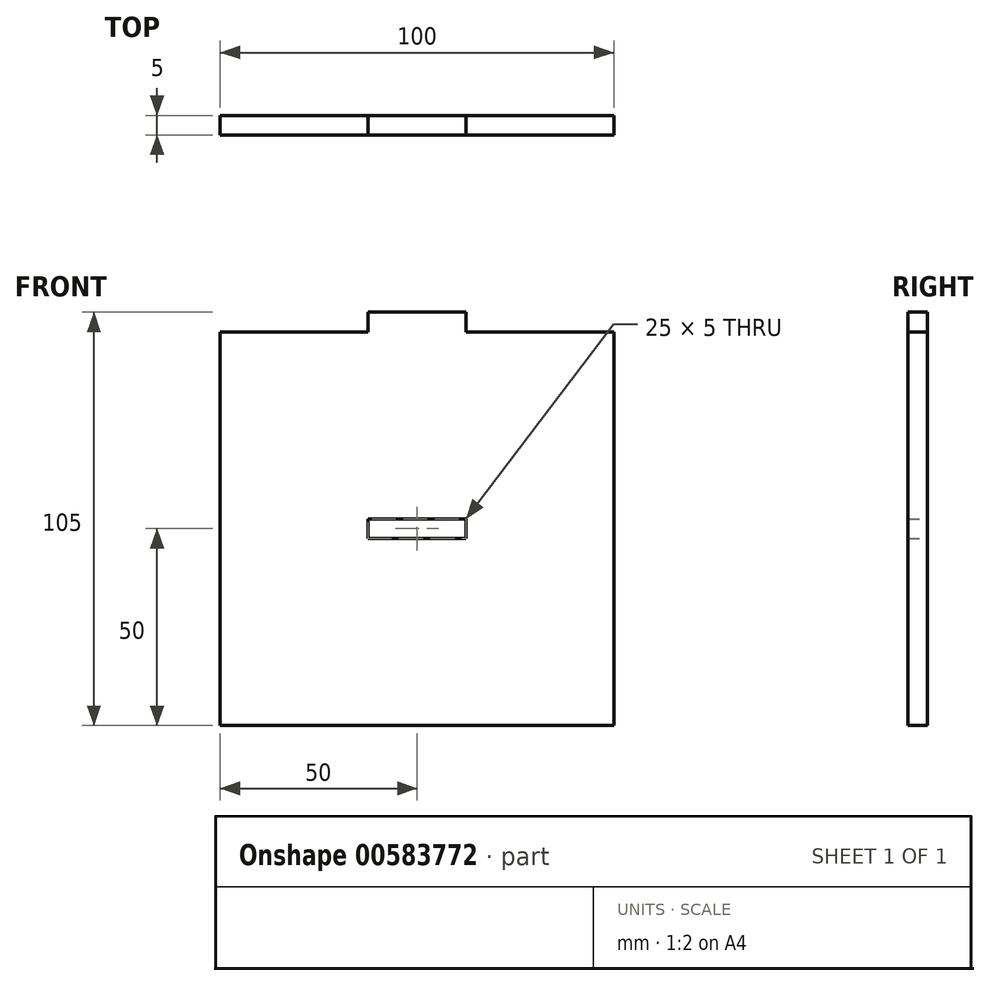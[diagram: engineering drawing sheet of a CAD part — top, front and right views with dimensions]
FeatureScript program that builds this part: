
annotation { "Feature Type Name" : "Feature", "Feature Type Description" : "" }
export const myFeature = defineFeature(function(context is Context, id is Id, definition is map)
    precondition{}
    {
        {
            var Q0;
            Q0=qCreatedBy(makeId("Front.planeOp"),FACE);
            var sketch = newSketch(context, id + "F0", { "sketchPlane" : qUnion([Q0])});
            skLineSegment(sketch, "E0", {"start": v(-62.5, 52.5) * mm, "end": v(-62.5, -47.5) * mm});
            skLineSegment(sketch, "E1", {"start": v(-62.5, -47.5) * mm, "end": v(37.5, -47.5) * mm});
            skLineSegment(sketch, "E2", {"start": v(37.5, -47.5) * mm, "end": v(37.5, 52.5) * mm});
            skLineSegment(sketch, "E3", {"start": v(37.5, 52.5) * mm, "end": v(0, 52.5) * mm});
            skLineSegment(sketch, "E4", {"start": v(0, 52.5) * mm, "end": v(0, 57.5) * mm});
            skLineSegment(sketch, "E5", {"start": v(0, 57.5) * mm, "end": v(-25, 57.5) * mm});
            skLineSegment(sketch, "E6", {"start": v(-25, 57.5) * mm, "end": v(-25, 52.5) * mm});
            skLineSegment(sketch, "E7", {"start": v(-25, 52.5) * mm, "end": v(-62.5, 52.5) * mm});
            skLineSegment(sketch, "E8.left", {"start": v(-58.91, 2.5) * mm, "end": v(-58.91, 2.5) * mm});
            skLineSegment(sketch, "E8.right", {"start": v(-66.09, 2.5) * mm, "end": v(-66.09, 2.5) * mm});
            skPoint(sketch, "E8.middle", {"position": v(-62.5, 2.5) * mm});
            skPoint(sketch, "E8.cornerSnap0", {"position": v(-62.5, 2.5) * mm});
            skLineSegment(sketch, "E9.bottom", {"start": v(0, 0) * mm, "end": v(-25, 0) * mm});
            skLineSegment(sketch, "E9.top", {"start": v(0, 5) * mm, "end": v(-25, 5) * mm});
            skLineSegment(sketch, "E9.left", {"start": v(0, 0) * mm, "end": v(0, 5) * mm});
            skLineSegment(sketch, "E9.right", {"start": v(-25, 0) * mm, "end": v(-25, 5) * mm});
            skPoint(sketch, "E9.middle", {"position": v(-12.5, 2.5) * mm});
            skPoint(sketch, "E9.middle.positionSnap0", {"position": v(-12.5, 57.5) * mm});
            skPoint(sketch, "E9.centerSnap0", {"position": v(-12.5, 57.5) * mm});
            skSolve(sketch);
        }
        {
            var Q0;
            Q0=makeQuery(id+"F0.imprint","IMPRINT",FACE,{"disambiguationData":[TD([[makeQuery(id+"F0.imprint","IMPRINT",EDGE,{"derivedFrom":sQuery(id+"F0.wireOp",EDGE,"E0")}),1.0]])]});
            extrude(context, id + "F1", {"entities" : qUnion([Q0]), "depth" : 5 * mm, "offsetDistance" : 25 * mm});
        }
    });
